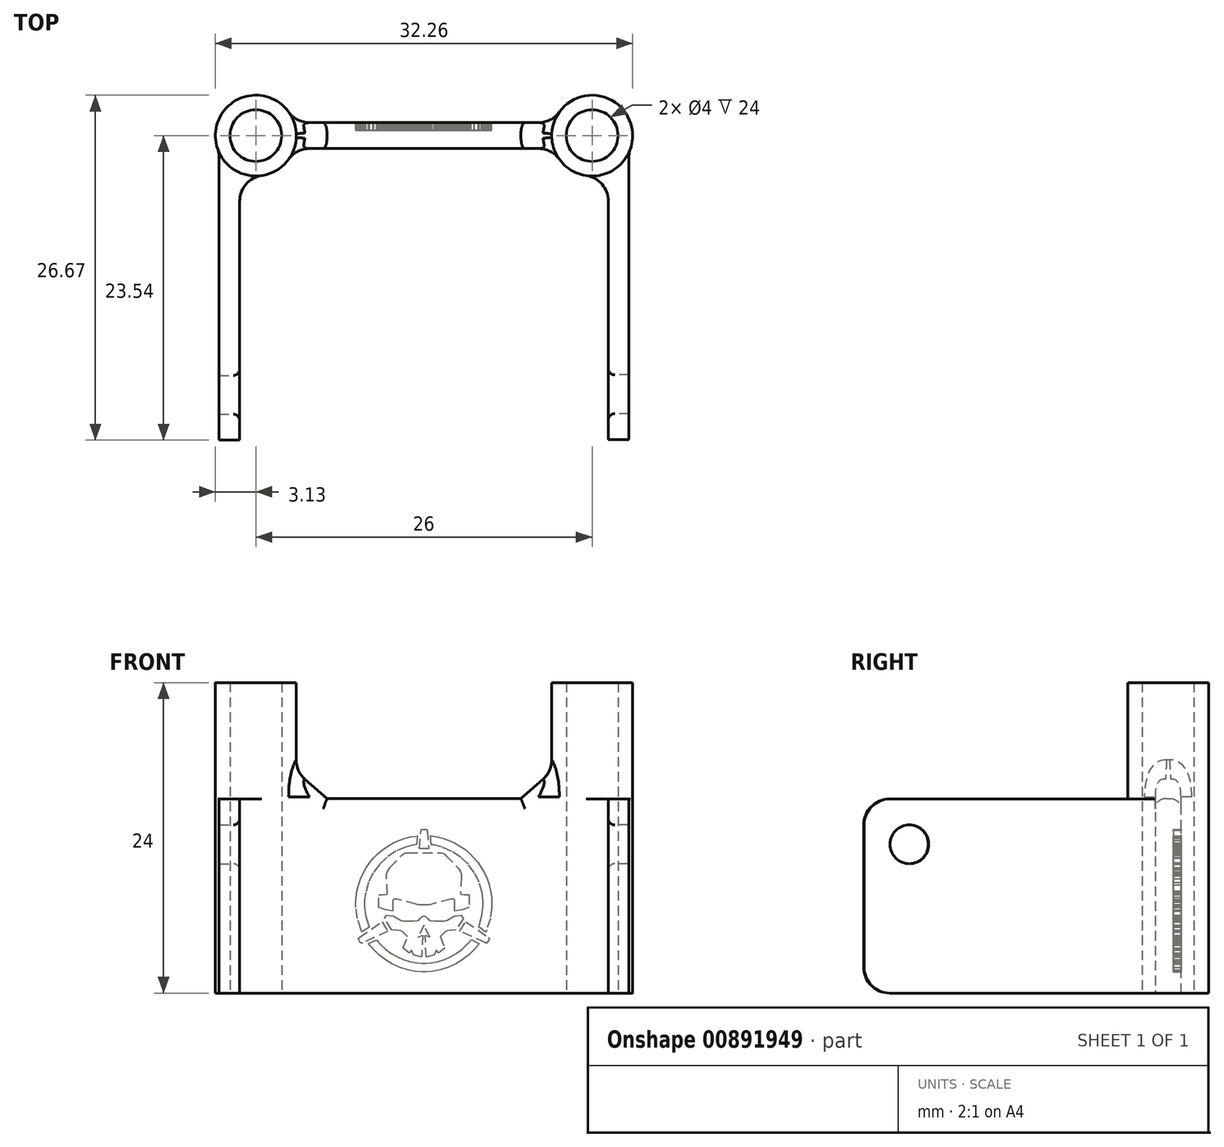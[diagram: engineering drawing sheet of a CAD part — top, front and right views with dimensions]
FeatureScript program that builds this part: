
annotation { "Feature Type Name" : "Feature", "Feature Type Description" : "" }
export const myFeature = defineFeature(function(context is Context, id is Id, definition is map)
    precondition{}
    {
        {
            var Q0;
            Q0=qCreatedBy(makeId("Top.planeOp"),FACE);
            var sketch = newSketch(context, id + "F0", { "sketchPlane" : qUnion([Q0])});
            skCircle(sketch, "E0", {"center": v(-13, 0) * mm, "radius": 3.12 * mm});
            skCircle(sketch, "E1", {"center": v(13, 0) * mm, "radius": 3.12 * mm});
            skSolve(sketch);
        }
        {
            var Q0;
            Q0=qSketchRegion(id+"F0",true);
            extrude(context, id + "F1", {"entities" : qUnion([Q0]), "depth" : 24 * mm});
        }
        {
            var Q0;
            Q0=qCreatedBy(makeId("Front.planeOp"),FACE);
            var sketch = newSketch(context, id + "F2", { "sketchPlane" : qUnion([Q0])});
            skLineSegment(sketch, "E2", {"start": v(12, 0) * mm, "end": v(12, 19) * mm});
            skLineSegment(sketch, "E3", {"start": v(12, 19) * mm, "end": v(12, 19) * mm});
            skLineSegment(sketch, "E4", {"start": v(12, 19) * mm, "end": v(7.5, 15.03) * mm});
            skLineSegment(sketch, "E5", {"start": v(7.5, 15.03) * mm, "end": v(-7.5, 15.03) * mm});
            skLineSegment(sketch, "E6", {"start": v(-7.5, 15.03) * mm, "end": v(-12, 19) * mm});
            skLineSegment(sketch, "E7", {"start": v(-12, 19) * mm, "end": v(-12, 0) * mm});
            skLineSegment(sketch, "E8", {"start": v(-12, 0) * mm, "end": v(12, 0) * mm});
            skSolve(sketch);
        }
        {
            var Q0;
            Q0=makeQuery(id+"F2.imprint","IMPRINT",FACE,{"disambiguationData":[TD([[makeQuery(id+"F2.imprint","IMPRINT",EDGE,{"derivedFrom":sQuery(id+"F2.wireOp",EDGE,"E2")}),1.0]])]});
            extrude(context, id + "F3", {"entities" : qUnion([Q0]), "depth" : 2 * mm, "symmetric" : true});
        }
        {
            var Q0;
            Q0=qCreatedBy(makeId("Right.planeOp"),FACE);
            var Q1;
            Q1=qBodyType(qCreatedBy(id+"F5",EDGE),BodyType.WIRE);
            cPlane(context, id + "F4", {"entities" : qUnion([Q0, Q1]), "cplaneType" : CPlaneType.OFFSET, "offset" : 14.25 * mm, "width" : 150 * mm, "height" : 150 * mm});
        }
        {
            var Q0;
            Q0=qCreatedBy(id+"F4.planeOp",FACE);
            var sketch = newSketch(context, id + "F5", { "sketchPlane" : qUnion([Q0])});
            skCircle(sketch, "E9", {"center": v(-20, 11.5) * mm, "radius": 1.5 * mm});
            skLineSegment(sketch, "E10", {"start": v(0, 0) * mm, "end": v(-21.5, 0) * mm});
            skLineSegment(sketch, "E11", {"start": v(-23.5, 2) * mm, "end": v(-23.5, 13) * mm});
            skLineSegment(sketch, "E12", {"start": v(-21.5, 15) * mm, "end": v(0, 15) * mm});
            skLineSegment(sketch, "E13", {"start": v(0, 15) * mm, "end": v(0, 0) * mm});
            skPoint(sketch, "E14.visualSharp", {"position": v(-23.5, 15) * mm});
            skArc(sketch, "E14.filletArc", {"start": v(-21.5, 15) * mm, "mid": v(-22.91, 14.41) * mm, "end": v(-23.5, 13) * mm});
            skPoint(sketch, "E15.visualSharp", {"position": v(-23.5, 0) * mm});
            skArc(sketch, "E15.filletArc", {"start": v(-23.5, 2) * mm, "mid": v(-22.91, 0.59) * mm, "end": v(-21.5, 0) * mm});
            skSolve(sketch);
        }
        {
            var Q0;
            Q0=qSketchRegion(id+"F5",true);
            extrude(context, id + "F6", {"entities" : qUnion([Q0]), "operationType" : NewBodyOperationType.ADD, "depth" : 1.6 * mm});
        }
        {
            var Q0;
            Q0=qCreatedBy(makeId("Right.planeOp"),FACE);
            cPlane(context, id + "F7", {"entities" : qUnion([Q0]), "cplaneType" : CPlaneType.OFFSET, "offset" : 14.25 * mm, "oppositeDirection" : true, "width" : 150 * mm, "height" : 150 * mm});
        }
        {
            var Q0;
            Q0=qCreatedBy(id+"F7.planeOp",FACE);
            var sketch = newSketch(context, id + "F8", { "sketchPlane" : qUnion([Q0])});
            skCircle(sketch, "E16", {"center": v(-20.04, 11.5) * mm, "radius": 1.5 * mm});
            skLineSegment(sketch, "E17", {"start": v(-0.04, 0) * mm, "end": v(-21.54, 0) * mm});
            skLineSegment(sketch, "E18", {"start": v(-23.54, 2) * mm, "end": v(-23.54, 13) * mm});
            skLineSegment(sketch, "E19", {"start": v(-21.54, 15) * mm, "end": v(-0.04, 15) * mm});
            skLineSegment(sketch, "E20", {"start": v(-0.04, 15) * mm, "end": v(-0.04, 0) * mm});
            skPoint(sketch, "E21.visualSharp", {"position": v(-23.54, 15) * mm});
            skArc(sketch, "E21.filletArc", {"start": v(-21.54, 15) * mm, "mid": v(-22.95, 14.41) * mm, "end": v(-23.54, 13) * mm});
            skPoint(sketch, "E22.visualSharp", {"position": v(-23.54, 0) * mm});
            skArc(sketch, "E22.filletArc", {"start": v(-23.54, 2) * mm, "mid": v(-22.95, 0.59) * mm, "end": v(-21.54, 0) * mm});
            skSolve(sketch);
        }
        {
            var Q0;
            Q0=qSketchRegion(id+"F8",true);
            extrude(context, id + "F9", {"entities" : qUnion([Q0]), "operationType" : NewBodyOperationType.ADD, "oppositeDirection" : true, "depth" : 1.6 * mm});
        }
        {
            var Q0;
            Q0=qCreatedBy(makeId("Top.planeOp"),FACE);
            var sketch = newSketch(context, id + "F10", { "sketchPlane" : qUnion([Q0])});
            skCircle(sketch, "E23", {"center": v(-13, 0) * mm, "radius": 0.5 * mm});
            skCircle(sketch, "E24", {"center": v(13, 0) * mm, "radius": 1.75 * mm});
            skSolve(sketch);
        }
        {
            var Q0;
            Q0=sQuery(id+"F10.wireOp",VERTEX,"E23.center");
            var Q1;
            Q1=sQuery(id+"F10.wireOp",VERTEX,"E24.center");
            var Q2;
            Q2=makeQuery(id+"F1.opExtrude","SWEPT_BODY",BODY,{"disambiguationData":[OSD([sQuery(id+"F0.wireOp",EDGE,"E0")])]});
            var Q3;
            Q3=makeQuery(id+"F3.opExtrude","SWEPT_BODY",BODY,{"disambiguationData":[OSD([sQuery(id+"F2.wireOp",EDGE,"in345Lub-D59E-tOme-60dj-Cq3KucnByxKd"),sQuery(id+"F2.wireOp",EDGE,"E2"),sQuery(id+"F2.wireOp",EDGE,"E4"),sQuery(id+"F2.wireOp",EDGE,"E5"),sQuery(id+"F2.wireOp",EDGE,"E6"),sQuery(id+"F2.wireOp",EDGE,"E7")])]});
            var Q4;
            Q4=makeQuery(id+"FYRTTrcSvXfLMjP_3.opExtrude","SWEPT_BODY",BODY,{"disambiguationData":[OSD([sQuery(id+"Fs8EBPNxBlUYa75_3.wireOp",EDGE,"JWLeMf17-8jiZ-tYXv-UtJK-ccR32AaEOkmf.bottom"),sQuery(id+"Fs8EBPNxBlUYa75_3.wireOp",EDGE,"JWLeMf17-8jiZ-tYXv-UtJK-ccR32AaEOkmf.top"),sQuery(id+"Fs8EBPNxBlUYa75_3.wireOp",EDGE,"JWLeMf17-8jiZ-tYXv-UtJK-ccR32AaEOkmf.left"),sQuery(id+"Fs8EBPNxBlUYa75_3.wireOp",EDGE,"JWLeMf17-8jiZ-tYXv-UtJK-ccR32AaEOkmf.right")])]});
            var Q5;
            Q5=makeQuery(id+"F1.opExtrude","SWEPT_BODY",BODY,{"disambiguationData":[OSD([sQuery(id+"F0.wireOp",EDGE,"E1")])]});
            var Q6;
            Q6=makeQuery(id+"FYRTTrcSvXfLMjP_3.opExtrude","SWEPT_BODY",BODY,{"disambiguationData":[OSD([sQuery(id+"Fs8EBPNxBlUYa75_3.wireOp",EDGE,"dHJZYZbQ-VqZX-6sAW-GdeU-ZCC2gI22Ho79.bottom"),sQuery(id+"Fs8EBPNxBlUYa75_3.wireOp",EDGE,"dHJZYZbQ-VqZX-6sAW-GdeU-ZCC2gI22Ho79.top"),sQuery(id+"Fs8EBPNxBlUYa75_3.wireOp",EDGE,"dHJZYZbQ-VqZX-6sAW-GdeU-ZCC2gI22Ho79.left"),sQuery(id+"Fs8EBPNxBlUYa75_3.wireOp",EDGE,"dHJZYZbQ-VqZX-6sAW-GdeU-ZCC2gI22Ho79.right")])]});
            hole(context, id + "F11", {"style" : HoleStyle.SIMPLE, "endStyle" : HoleEndStyle.THROUGH, "oppositeDirection" : true, "holeDiameter" : 4 * mm, "isTappedThrough" : true, "tappedDepth" : 12 * mm, "tapClearance" : 3, "locations" : qUnion([Q0, Q1]), "scope" : qUnion([Q2, Q3, Q4, Q5, Q6])});
        }
        {
            var Q0;
            Q0=makeQuery(id+"F1.opExtrude","SWEPT_BODY",BODY,{"disambiguationData":[OSD([sQuery(id+"F0.wireOp",EDGE,"E1")])]});
            var Q1;
            Q1=makeQuery(id+"F3.opExtrude","SWEPT_BODY",BODY,{"disambiguationData":[OSD([sQuery(id+"F2.wireOp",EDGE,"in345Lub-D59E-tOme-60dj-Cq3KucnByxKd"),sQuery(id+"F2.wireOp",EDGE,"E2"),sQuery(id+"F2.wireOp",EDGE,"E4"),sQuery(id+"F2.wireOp",EDGE,"E5"),sQuery(id+"F2.wireOp",EDGE,"E6"),sQuery(id+"F2.wireOp",EDGE,"E7")])]});
            var Q2;
            Q2=makeQuery(id+"F1.opExtrude","SWEPT_BODY",BODY,{"disambiguationData":[OSD([sQuery(id+"F0.wireOp",EDGE,"E0")])]});
            booleanBodies(context, id + "F12", {"operationType" : BooleanOperationType.UNION, "tools" : qUnion([Q0, Q1, Q2])});
        }
        {
            var Q0;
            Q0=makeQuery(id+"F3.opExtrude","CAP_EDGE",EDGE,{"disambiguationData":[OSD([sQuery(id+"F2.wireOp",EDGE,"E5")])],"isStart":false});
            var Q1;
            Q1=makeQuery(id+"F3.opExtrude","CAP_EDGE",EDGE,{"disambiguationData":[OSD([sQuery(id+"F2.wireOp",EDGE,"E5")])],"isStart":true});
            var Q2;
            Q2=makeQuery(id+"F3.opExtrude","CAP_EDGE",EDGE,{"disambiguationData":[OSD([sQuery(id+"F2.wireOp",EDGE,"E6")])],"isStart":false});
            var Q3;
            Q3=makeQuery(id+"F3.opExtrude","CAP_EDGE",EDGE,{"disambiguationData":[OSD([sQuery(id+"F2.wireOp",EDGE,"E6")])],"isStart":true});
            var Q4;
            Q4=makeQuery(id+"F3.opExtrude","CAP_EDGE",EDGE,{"disambiguationData":[OSD([sQuery(id+"F2.wireOp",EDGE,"E4")])],"isStart":false});
            var Q5;
            Q5=makeQuery(id+"F3.opExtrude","CAP_EDGE",EDGE,{"disambiguationData":[OSD([sQuery(id+"F2.wireOp",EDGE,"E4")])],"isStart":true});
            fillet(context, id + "F13", {"entities" : qUnion([Q0, Q1, Q2, Q3, Q4, Q5]), "radius" : .8 * mm, "tangentPropagation" : true, "allowEdgeOverflow" : false});
        }
        {
            var Q0;
            Q0=makeQuery(id+"F11.hole-0.boolean.opBoolean","INTERSECT",EDGE,{"derivedFrom":[makeQuery(id+"F1.opExtrude","CAP_FACE",FACE,{"disambiguationData":[OSD([sQuery(id+"F0.wireOp",EDGE,"E0")])],"isStart":false}),makeQuery(id+"F11.hole-0.opRevolve","SWEPT_FACE",FACE,{"disambiguationData":[OSD([sQuery(id+"F11.hole-0.sketch.wireOp",EDGE,"core_line_2")])]})]});
            var Q1;
            Q1=makeQuery(id+"F11.hole-1.boolean.opBoolean","INTERSECT",EDGE,{"derivedFrom":[makeQuery(id+"F1.opExtrude","CAP_FACE",FACE,{"disambiguationData":[OSD([sQuery(id+"F0.wireOp",EDGE,"E1")])],"isStart":false}),makeQuery(id+"F11.hole-1.opRevolve","SWEPT_FACE",FACE,{"disambiguationData":[OSD([sQuery(id+"F11.hole-1.sketch.wireOp",EDGE,"core_line_2")])]})]});
            var Q2;
            Q2=makeQuery(id+"F9.opExtrude","CAP_EDGE",EDGE,{"disambiguationData":[OSD([sQuery(id+"F8.wireOp",EDGE,"E16")])],"isStart":true});
            var Q3;
            Q3=makeQuery(id+"F6.opExtrude","CAP_EDGE",EDGE,{"disambiguationData":[OSD([sQuery(id+"F5.wireOp",EDGE,"E9")])],"isStart":true});
            fillet(context, id + "F14", {"entities" : qUnion([Q0, Q1, Q2, Q3]), "radius" : .5 * mm, "tangentPropagation" : true, "allowEdgeOverflow" : false});
        }
        {
            var Q0;
            Q0=makeQuery(id+"F3.opExtrude","CAP_FACE",FACE,{"disambiguationData":[OSD([sQuery(id+"F2.wireOp",EDGE,"E2"),sQuery(id+"F2.wireOp",EDGE,"E4"),sQuery(id+"F2.wireOp",EDGE,"E5"),sQuery(id+"F2.wireOp",EDGE,"E6"),sQuery(id+"F2.wireOp",EDGE,"E7"),sQuery(id+"F2.wireOp",EDGE,"E8")])],"isStart":true});
            var sketch = newSketch(context, id + "F15", { "sketchPlane" : qUnion([Q0])});
            skLineSegment(sketch, "E25", {"start": v(-0.2, 12.65) * mm, "end": v(-0.2, 12.64) * mm});
            skLineSegment(sketch, "E26", {"start": v(-0.2, 12.64) * mm, "end": v(-0.23, 12.63) * mm});
            skLineSegment(sketch, "E27", {"start": v(-0.23, 12.63) * mm, "end": v(-0.24, 12.59) * mm});
            skLineSegment(sketch, "E28", {"start": v(-0.24, 12.59) * mm, "end": v(-0.24, 12.58) * mm});
            skLineSegment(sketch, "E29", {"start": v(-0.24, 12.58) * mm, "end": v(-0.38, 11.17) * mm});
            skLineSegment(sketch, "E30", {"start": v(-0.38, 11.17) * mm, "end": v(0.36, 11.17) * mm});
            skLineSegment(sketch, "E31", {"start": v(0.36, 11.17) * mm, "end": v(0.22, 12.58) * mm});
            skLineSegment(sketch, "E32", {"start": v(0.22, 12.58) * mm, "end": v(0.22, 12.59) * mm});
            skLineSegment(sketch, "E33", {"start": v(0.22, 12.59) * mm, "end": v(0.2, 12.63) * mm});
            skLineSegment(sketch, "E34", {"start": v(0.2, 12.63) * mm, "end": v(0.19, 12.64) * mm});
            skLineSegment(sketch, "E35", {"start": v(0.19, 12.64) * mm, "end": v(0.18, 12.65) * mm});
            skLineSegment(sketch, "E36", {"start": v(0.18, 12.65) * mm, "end": v(-0.2, 12.65) * mm});
            skLineSegment(sketch, "E37", {"start": v(-0.5, 12.15) * mm, "end": v(-0.63, 12.13) * mm});
            skLineSegment(sketch, "E38", {"start": v(-0.63, 12.13) * mm, "end": v(-1, 12.07) * mm});
            skLineSegment(sketch, "E39", {"start": v(-1, 12.07) * mm, "end": v(-1.48, 11.96) * mm});
            skLineSegment(sketch, "E40", {"start": v(-1.48, 11.96) * mm, "end": v(-1.94, 11.8) * mm});
            skLineSegment(sketch, "E41", {"start": v(-1.94, 11.8) * mm, "end": v(-2.38, 11.6) * mm});
            skLineSegment(sketch, "E42", {"start": v(-2.38, 11.6) * mm, "end": v(-2.8, 11.36) * mm});
            skLineSegment(sketch, "E43", {"start": v(-2.8, 11.36) * mm, "end": v(-3.19, 11.09) * mm});
            skLineSegment(sketch, "E44", {"start": v(-3.19, 11.09) * mm, "end": v(-3.55, 10.78) * mm});
            skLineSegment(sketch, "E45", {"start": v(-3.55, 10.78) * mm, "end": v(-3.89, 10.44) * mm});
            skLineSegment(sketch, "E46", {"start": v(-3.89, 10.44) * mm, "end": v(-4.19, 10.08) * mm});
            skLineSegment(sketch, "E47", {"start": v(-4.19, 10.08) * mm, "end": v(-4.46, 9.69) * mm});
            skLineSegment(sketch, "E48", {"start": v(-4.46, 9.69) * mm, "end": v(-4.69, 9.27) * mm});
            skLineSegment(sketch, "E49", {"start": v(-4.69, 9.27) * mm, "end": v(-4.88, 8.83) * mm});
            skLineSegment(sketch, "E50", {"start": v(-4.88, 8.83) * mm, "end": v(-5.04, 8.38) * mm});
            skLineSegment(sketch, "E51", {"start": v(-5.04, 8.38) * mm, "end": v(-5.15, 7.9) * mm});
            skLineSegment(sketch, "E52", {"start": v(-5.15, 7.9) * mm, "end": v(-5.22, 7.41) * mm});
            skLineSegment(sketch, "E53", {"start": v(-5.22, 7.41) * mm, "end": v(-5.25, 7.04) * mm});
            skLineSegment(sketch, "E54", {"start": v(-5.25, 7.04) * mm, "end": v(-5.25, 6.9) * mm});
            skLineSegment(sketch, "E55", {"start": v(-5.25, 6.9) * mm, "end": v(-5.25, 6.63) * mm});
            skLineSegment(sketch, "E56", {"start": v(-5.25, 6.63) * mm, "end": v(-5.12, 5.77) * mm});
            skLineSegment(sketch, "E57", {"start": v(-5.12, 5.77) * mm, "end": v(-4.85, 4.89) * mm});
            skLineSegment(sketch, "E58", {"start": v(-4.85, 4.89) * mm, "end": v(-4.77, 4.72) * mm});
            skLineSegment(sketch, "E59", {"start": v(-4.77, 4.72) * mm, "end": v(-4.22, 5.12) * mm});
            skLineSegment(sketch, "E60", {"start": v(-4.22, 5.12) * mm, "end": v(-4.28, 5.25) * mm});
            skLineSegment(sketch, "E61", {"start": v(-4.28, 5.25) * mm, "end": v(-4.49, 5.98) * mm});
            skLineSegment(sketch, "E62", {"start": v(-4.49, 5.98) * mm, "end": v(-4.58, 6.68) * mm});
            skLineSegment(sketch, "E63", {"start": v(-4.58, 6.68) * mm, "end": v(-4.58, 6.9) * mm});
            skLineSegment(sketch, "E64", {"start": v(-4.58, 6.9) * mm, "end": v(-4.58, 7.12) * mm});
            skLineSegment(sketch, "E65", {"start": v(-4.58, 7.12) * mm, "end": v(-4.5, 7.76) * mm});
            skLineSegment(sketch, "E66", {"start": v(-4.5, 7.76) * mm, "end": v(-4.28, 8.56) * mm});
            skLineSegment(sketch, "E67", {"start": v(-4.28, 8.56) * mm, "end": v(-3.91, 9.3) * mm});
            skLineSegment(sketch, "E68", {"start": v(-3.91, 9.3) * mm, "end": v(-3.43, 9.95) * mm});
            skLineSegment(sketch, "E69", {"start": v(-3.43, 9.95) * mm, "end": v(-2.84, 10.5) * mm});
            skLineSegment(sketch, "E70", {"start": v(-2.84, 10.5) * mm, "end": v(-2.16, 10.96) * mm});
            skLineSegment(sketch, "E71", {"start": v(-2.16, 10.96) * mm, "end": v(-1.4, 11.28) * mm});
            skLineSegment(sketch, "E72", {"start": v(-1.4, 11.28) * mm, "end": v(-0.78, 11.44) * mm});
            skLineSegment(sketch, "E73", {"start": v(-0.78, 11.44) * mm, "end": v(-0.57, 11.46) * mm});
            skLineSegment(sketch, "E74", {"start": v(-0.57, 11.46) * mm, "end": v(-0.5, 12.15) * mm});
            skLineSegment(sketch, "E75", {"start": v(0.52, 12.14) * mm, "end": v(0.58, 11.47) * mm});
            skLineSegment(sketch, "E76", {"start": v(0.58, 11.47) * mm, "end": v(0.79, 11.44) * mm});
            skLineSegment(sketch, "E77", {"start": v(0.79, 11.44) * mm, "end": v(1.4, 11.28) * mm});
            skLineSegment(sketch, "E78", {"start": v(1.4, 11.28) * mm, "end": v(2.17, 10.96) * mm});
            skLineSegment(sketch, "E79", {"start": v(2.17, 10.96) * mm, "end": v(2.86, 10.5) * mm});
            skLineSegment(sketch, "E80", {"start": v(2.86, 10.5) * mm, "end": v(3.45, 9.95) * mm});
            skLineSegment(sketch, "E81", {"start": v(3.45, 9.95) * mm, "end": v(3.93, 9.3) * mm});
            skLineSegment(sketch, "E82", {"start": v(3.93, 9.3) * mm, "end": v(4.3, 8.56) * mm});
            skLineSegment(sketch, "E83", {"start": v(4.3, 8.56) * mm, "end": v(4.52, 7.76) * mm});
            skLineSegment(sketch, "E84", {"start": v(4.52, 7.76) * mm, "end": v(4.6, 7.12) * mm});
            skLineSegment(sketch, "E85", {"start": v(4.6, 7.12) * mm, "end": v(4.6, 6.9) * mm});
            skLineSegment(sketch, "E86", {"start": v(4.6, 6.9) * mm, "end": v(4.6, 6.68) * mm});
            skLineSegment(sketch, "E87", {"start": v(4.6, 6.68) * mm, "end": v(4.5, 5.98) * mm});
            skLineSegment(sketch, "E88", {"start": v(4.5, 5.98) * mm, "end": v(4.3, 5.25) * mm});
            skLineSegment(sketch, "E89", {"start": v(4.3, 5.25) * mm, "end": v(4.23, 5.11) * mm});
            skLineSegment(sketch, "E90", {"start": v(4.23, 5.11) * mm, "end": v(4.78, 4.71) * mm});
            skLineSegment(sketch, "E91", {"start": v(4.78, 4.71) * mm, "end": v(4.86, 4.88) * mm});
            skLineSegment(sketch, "E92", {"start": v(4.86, 4.88) * mm, "end": v(5.14, 5.77) * mm});
            skLineSegment(sketch, "E93", {"start": v(5.14, 5.77) * mm, "end": v(5.26, 6.62) * mm});
            skLineSegment(sketch, "E94", {"start": v(5.26, 6.62) * mm, "end": v(5.26, 6.9) * mm});
            skLineSegment(sketch, "E95", {"start": v(5.26, 6.9) * mm, "end": v(5.26, 7.04) * mm});
            skLineSegment(sketch, "E96", {"start": v(5.26, 7.04) * mm, "end": v(5.24, 7.41) * mm});
            skLineSegment(sketch, "E97", {"start": v(5.24, 7.41) * mm, "end": v(5.17, 7.9) * mm});
            skLineSegment(sketch, "E98", {"start": v(5.17, 7.9) * mm, "end": v(5.05, 8.37) * mm});
            skLineSegment(sketch, "E99", {"start": v(5.05, 8.37) * mm, "end": v(4.9, 8.83) * mm});
            skLineSegment(sketch, "E100", {"start": v(4.9, 8.83) * mm, "end": v(4.7, 9.27) * mm});
            skLineSegment(sketch, "E101", {"start": v(4.7, 9.27) * mm, "end": v(4.47, 9.68) * mm});
            skLineSegment(sketch, "E102", {"start": v(4.47, 9.68) * mm, "end": v(4.2, 10.08) * mm});
            skLineSegment(sketch, "E103", {"start": v(4.2, 10.08) * mm, "end": v(3.9, 10.44) * mm});
            skLineSegment(sketch, "E104", {"start": v(3.9, 10.44) * mm, "end": v(3.56, 10.78) * mm});
            skLineSegment(sketch, "E105", {"start": v(3.56, 10.78) * mm, "end": v(3.2, 11.08) * mm});
            skLineSegment(sketch, "E106", {"start": v(3.2, 11.08) * mm, "end": v(2.8, 11.36) * mm});
            skLineSegment(sketch, "E107", {"start": v(2.8, 11.36) * mm, "end": v(2.4, 11.6) * mm});
            skLineSegment(sketch, "E108", {"start": v(2.4, 11.6) * mm, "end": v(1.95, 11.8) * mm});
            skLineSegment(sketch, "E109", {"start": v(1.95, 11.8) * mm, "end": v(1.5, 11.95) * mm});
            skLineSegment(sketch, "E110", {"start": v(1.5, 11.95) * mm, "end": v(1.01, 12.07) * mm});
            skLineSegment(sketch, "E111", {"start": v(1.01, 12.07) * mm, "end": v(0.64, 12.13) * mm});
            skLineSegment(sketch, "E112", {"start": v(0.64, 12.13) * mm, "end": v(0.52, 12.14) * mm});
            skLineSegment(sketch, "E113", {"start": v(-1.2, 10.86) * mm, "end": v(-1.23, 10.86) * mm});
            skLineSegment(sketch, "E114", {"start": v(-1.23, 10.86) * mm, "end": v(-1.34, 10.84) * mm});
            skLineSegment(sketch, "E115", {"start": v(-1.34, 10.84) * mm, "end": v(-1.47, 10.8) * mm});
            skLineSegment(sketch, "E116", {"start": v(-1.47, 10.8) * mm, "end": v(-1.59, 10.75) * mm});
            skLineSegment(sketch, "E117", {"start": v(-1.59, 10.75) * mm, "end": v(-1.66, 10.69) * mm});
            skLineSegment(sketch, "E118", {"start": v(-1.66, 10.69) * mm, "end": v(-1.69, 10.66) * mm});
            skLineSegment(sketch, "E119", {"start": v(-1.69, 10.66) * mm, "end": v(-2.61, 9.7) * mm});
            skLineSegment(sketch, "E120", {"start": v(-2.61, 9.7) * mm, "end": v(-2.64, 9.67) * mm});
            skLineSegment(sketch, "E121", {"start": v(-2.64, 9.67) * mm, "end": v(-2.72, 9.56) * mm});
            skLineSegment(sketch, "E122", {"start": v(-2.72, 9.56) * mm, "end": v(-2.81, 9.39) * mm});
            skLineSegment(sketch, "E123", {"start": v(-2.81, 9.39) * mm, "end": v(-2.87, 9.2) * mm});
            skLineSegment(sketch, "E124", {"start": v(-2.87, 9.2) * mm, "end": v(-2.9, 9.05) * mm});
            skLineSegment(sketch, "E125", {"start": v(-2.9, 9.05) * mm, "end": v(-2.9, 9) * mm});
            skLineSegment(sketch, "E126", {"start": v(-2.9, 9) * mm, "end": v(-2.82, 7.67) * mm});
            skLineSegment(sketch, "E127", {"start": v(-2.82, 7.67) * mm, "end": v(-2.87, 7.65) * mm});
            skLineSegment(sketch, "E128", {"start": v(-2.87, 7.65) * mm, "end": v(-3.14, 7.6) * mm});
            skLineSegment(sketch, "E129", {"start": v(-3.14, 7.6) * mm, "end": v(-3.42, 7.6) * mm});
            skLineSegment(sketch, "E130", {"start": v(-3.42, 7.6) * mm, "end": v(-3.48, 7.6) * mm});
            skLineSegment(sketch, "E131", {"start": v(-3.48, 7.6) * mm, "end": v(-3.48, 6.61) * mm});
            skLineSegment(sketch, "E132", {"start": v(-3.48, 6.61) * mm, "end": v(-2.94, 6.42) * mm});
            skLineSegment(sketch, "E133", {"start": v(-2.94, 6.42) * mm, "end": v(-2.4, 6.35) * mm});
            skLineSegment(sketch, "E134", {"start": v(-2.4, 6.35) * mm, "end": v(-2.4, 7.11) * mm});
            skLineSegment(sketch, "E135", {"start": v(-2.4, 7.11) * mm, "end": v(-2.4, 7.13) * mm});
            skLineSegment(sketch, "E136", {"start": v(-2.4, 7.13) * mm, "end": v(-2.37, 7.2) * mm});
            skLineSegment(sketch, "E137", {"start": v(-2.37, 7.2) * mm, "end": v(-2.31, 7.25) * mm});
            skLineSegment(sketch, "E138", {"start": v(-2.31, 7.25) * mm, "end": v(-2.21, 7.27) * mm});
            skLineSegment(sketch, "E139", {"start": v(-2.21, 7.27) * mm, "end": v(-2.1, 7.27) * mm});
            skLineSegment(sketch, "E140", {"start": v(-2.1, 7.27) * mm, "end": v(-2.07, 7.26) * mm});
            skLineSegment(sketch, "E141", {"start": v(-2.07, 7.26) * mm, "end": v(-0.6, 6.87) * mm});
            skLineSegment(sketch, "E142", {"start": v(-0.6, 6.87) * mm, "end": v(-0.57, 6.86) * mm});
            skLineSegment(sketch, "E143", {"start": v(-0.57, 6.86) * mm, "end": v(-0.4, 6.82) * mm});
            skLineSegment(sketch, "E144", {"start": v(-0.4, 6.82) * mm, "end": v(-0.27, 6.8) * mm});
            skLineSegment(sketch, "E145", {"start": v(-0.27, 6.8) * mm, "end": v(-0.23, 6.8) * mm});
            skLineSegment(sketch, "E146", {"start": v(-0.23, 6.8) * mm, "end": v(0.24, 6.8) * mm});
            skLineSegment(sketch, "E147", {"start": v(0.24, 6.8) * mm, "end": v(0.29, 6.8) * mm});
            skLineSegment(sketch, "E148", {"start": v(0.29, 6.8) * mm, "end": v(0.42, 6.82) * mm});
            skLineSegment(sketch, "E149", {"start": v(0.42, 6.82) * mm, "end": v(0.58, 6.86) * mm});
            skLineSegment(sketch, "E150", {"start": v(0.58, 6.86) * mm, "end": v(0.61, 6.87) * mm});
            skLineSegment(sketch, "E151", {"start": v(0.61, 6.87) * mm, "end": v(2.08, 7.26) * mm});
            skLineSegment(sketch, "E152", {"start": v(2.08, 7.26) * mm, "end": v(2.12, 7.27) * mm});
            skLineSegment(sketch, "E153", {"start": v(2.12, 7.27) * mm, "end": v(2.23, 7.27) * mm});
            skLineSegment(sketch, "E154", {"start": v(2.23, 7.27) * mm, "end": v(2.33, 7.25) * mm});
            skLineSegment(sketch, "E155", {"start": v(2.33, 7.25) * mm, "end": v(2.39, 7.2) * mm});
            skLineSegment(sketch, "E156", {"start": v(2.39, 7.2) * mm, "end": v(2.4, 7.13) * mm});
            skLineSegment(sketch, "E157", {"start": v(2.4, 7.13) * mm, "end": v(2.4, 7.11) * mm});
            skLineSegment(sketch, "E158", {"start": v(2.4, 7.11) * mm, "end": v(2.4, 6.35) * mm});
            skLineSegment(sketch, "E159", {"start": v(2.4, 6.35) * mm, "end": v(2.96, 6.42) * mm});
            skLineSegment(sketch, "E160", {"start": v(2.96, 6.42) * mm, "end": v(3.5, 6.61) * mm});
            skLineSegment(sketch, "E161", {"start": v(3.5, 6.61) * mm, "end": v(3.5, 7.6) * mm});
            skLineSegment(sketch, "E162", {"start": v(3.5, 7.6) * mm, "end": v(3.44, 7.6) * mm});
            skLineSegment(sketch, "E163", {"start": v(3.44, 7.6) * mm, "end": v(3.16, 7.6) * mm});
            skLineSegment(sketch, "E164", {"start": v(3.16, 7.6) * mm, "end": v(2.89, 7.65) * mm});
            skLineSegment(sketch, "E165", {"start": v(2.89, 7.65) * mm, "end": v(2.84, 7.67) * mm});
            skLineSegment(sketch, "E166", {"start": v(2.84, 7.67) * mm, "end": v(2.9, 9) * mm});
            skLineSegment(sketch, "E167", {"start": v(2.9, 9) * mm, "end": v(2.9, 9.05) * mm});
            skLineSegment(sketch, "E168", {"start": v(2.9, 9.05) * mm, "end": v(2.89, 9.2) * mm});
            skLineSegment(sketch, "E169", {"start": v(2.89, 9.2) * mm, "end": v(2.83, 9.39) * mm});
            skLineSegment(sketch, "E170", {"start": v(2.83, 9.39) * mm, "end": v(2.73, 9.56) * mm});
            skLineSegment(sketch, "E171", {"start": v(2.73, 9.56) * mm, "end": v(2.66, 9.67) * mm});
            skLineSegment(sketch, "E172", {"start": v(2.66, 9.67) * mm, "end": v(2.63, 9.7) * mm});
            skLineSegment(sketch, "E173", {"start": v(2.63, 9.7) * mm, "end": v(1.7, 10.66) * mm});
            skLineSegment(sketch, "E174", {"start": v(1.7, 10.66) * mm, "end": v(1.68, 10.69) * mm});
            skLineSegment(sketch, "E175", {"start": v(1.68, 10.69) * mm, "end": v(1.6, 10.75) * mm});
            skLineSegment(sketch, "E176", {"start": v(1.6, 10.75) * mm, "end": v(1.49, 10.8) * mm});
            skLineSegment(sketch, "E177", {"start": v(1.49, 10.8) * mm, "end": v(1.36, 10.84) * mm});
            skLineSegment(sketch, "E178", {"start": v(1.36, 10.84) * mm, "end": v(1.24, 10.86) * mm});
            skLineSegment(sketch, "E179", {"start": v(1.24, 10.86) * mm, "end": v(1.2, 10.86) * mm});
            skLineSegment(sketch, "E180", {"start": v(1.2, 10.86) * mm, "end": v(-1.2, 10.86) * mm});
            skLineSegment(sketch, "E181", {"start": v(-2.87, 6.03) * mm, "end": v(-3.04, 5.77) * mm});
            skLineSegment(sketch, "E182", {"start": v(-3.04, 5.77) * mm, "end": v(-2.46, 4.87) * mm});
            skLineSegment(sketch, "E183", {"start": v(-2.46, 4.87) * mm, "end": v(-2.05, 4.85) * mm});
            skLineSegment(sketch, "E184", {"start": v(-2.05, 4.85) * mm, "end": v(-2, 4.85) * mm});
            skLineSegment(sketch, "E185", {"start": v(-2, 4.85) * mm, "end": v(-1.8, 4.83) * mm});
            skLineSegment(sketch, "E186", {"start": v(-1.8, 4.83) * mm, "end": v(-1.63, 4.76) * mm});
            skLineSegment(sketch, "E187", {"start": v(-1.63, 4.76) * mm, "end": v(-1.6, 4.73) * mm});
            skLineSegment(sketch, "E188", {"start": v(-1.6, 4.73) * mm, "end": v(-1.26, 4.38) * mm});
            skLineSegment(sketch, "E189", {"start": v(-1.26, 4.38) * mm, "end": v(-1.61, 3.48) * mm});
            skLineSegment(sketch, "E190", {"start": v(-1.61, 3.48) * mm, "end": v(-1.14, 3.1) * mm});
            skLineSegment(sketch, "E191", {"start": v(-1.14, 3.1) * mm, "end": v(-0.94, 3.31) * mm});
            skLineSegment(sketch, "E192", {"start": v(-0.94, 3.31) * mm, "end": v(-0.78, 2.93) * mm});
            skLineSegment(sketch, "E193", {"start": v(-0.78, 2.93) * mm, "end": v(-0.18, 2.77) * mm});
            skLineSegment(sketch, "E194", {"start": v(-0.18, 2.77) * mm, "end": v(-0.08, 4.48) * mm});
            skLineSegment(sketch, "E195", {"start": v(-0.08, 4.48) * mm, "end": v(-0.43, 4.33) * mm});
            skLineSegment(sketch, "E196", {"start": v(-0.43, 4.33) * mm, "end": v(0, 5.26) * mm});
            skLineSegment(sketch, "E197", {"start": v(0, 5.26) * mm, "end": v(0.45, 4.33) * mm});
            skLineSegment(sketch, "E198", {"start": v(0.45, 4.33) * mm, "end": v(0.1, 4.48) * mm});
            skLineSegment(sketch, "E199", {"start": v(0.1, 4.48) * mm, "end": v(0.2, 2.77) * mm});
            skLineSegment(sketch, "E200", {"start": v(0.2, 2.77) * mm, "end": v(0.8, 2.93) * mm});
            skLineSegment(sketch, "E201", {"start": v(0.8, 2.93) * mm, "end": v(0.95, 3.31) * mm});
            skLineSegment(sketch, "E202", {"start": v(0.95, 3.31) * mm, "end": v(1.15, 3.1) * mm});
            skLineSegment(sketch, "E203", {"start": v(1.15, 3.1) * mm, "end": v(1.63, 3.48) * mm});
            skLineSegment(sketch, "E204", {"start": v(1.63, 3.48) * mm, "end": v(1.27, 4.38) * mm});
            skLineSegment(sketch, "E205", {"start": v(1.27, 4.38) * mm, "end": v(1.62, 4.73) * mm});
            skLineSegment(sketch, "E206", {"start": v(1.62, 4.73) * mm, "end": v(1.65, 4.76) * mm});
            skLineSegment(sketch, "E207", {"start": v(1.65, 4.76) * mm, "end": v(1.82, 4.83) * mm});
            skLineSegment(sketch, "E208", {"start": v(1.82, 4.83) * mm, "end": v(2.02, 4.85) * mm});
            skLineSegment(sketch, "E209", {"start": v(2.02, 4.85) * mm, "end": v(2.07, 4.85) * mm});
            skLineSegment(sketch, "E210", {"start": v(2.07, 4.85) * mm, "end": v(2.48, 4.87) * mm});
            skLineSegment(sketch, "E211", {"start": v(2.48, 4.87) * mm, "end": v(3.06, 5.77) * mm});
            skLineSegment(sketch, "E212", {"start": v(3.06, 5.77) * mm, "end": v(2.88, 6.03) * mm});
            skLineSegment(sketch, "E213", {"start": v(2.88, 6.03) * mm, "end": v(2.35, 5.97) * mm});
            skLineSegment(sketch, "E214", {"start": v(2.35, 5.97) * mm, "end": v(1.82, 5.64) * mm});
            skLineSegment(sketch, "E215", {"start": v(1.82, 5.64) * mm, "end": v(1.75, 5.62) * mm});
            skLineSegment(sketch, "E216", {"start": v(1.75, 5.62) * mm, "end": v(1.53, 5.59) * mm});
            skLineSegment(sketch, "E217", {"start": v(1.53, 5.59) * mm, "end": v(1.2, 5.57) * mm});
            skLineSegment(sketch, "E218", {"start": v(1.2, 5.57) * mm, "end": v(0.83, 5.58) * mm});
            skLineSegment(sketch, "E219", {"start": v(0.83, 5.58) * mm, "end": v(0.5, 5.61) * mm});
            skLineSegment(sketch, "E220", {"start": v(0.5, 5.61) * mm, "end": v(0.4, 5.63) * mm});
            skLineSegment(sketch, "E221", {"start": v(0.4, 5.63) * mm, "end": v(0.38, 5.65) * mm});
            skLineSegment(sketch, "E222", {"start": v(0.38, 5.65) * mm, "end": v(0.33, 5.73) * mm});
            skLineSegment(sketch, "E223", {"start": v(0.33, 5.73) * mm, "end": v(0.23, 5.84) * mm});
            skLineSegment(sketch, "E224", {"start": v(0.23, 5.84) * mm, "end": v(0.12, 5.93) * mm});
            skLineSegment(sketch, "E225", {"start": v(0.12, 5.93) * mm, "end": v(0.04, 5.96) * mm});
            skLineSegment(sketch, "E226", {"start": v(0.04, 5.96) * mm, "end": v(0, 5.96) * mm});
            skLineSegment(sketch, "E227", {"start": v(0, 5.96) * mm, "end": v(-0.02, 5.96) * mm});
            skLineSegment(sketch, "E228", {"start": v(-0.02, 5.96) * mm, "end": v(-0.1, 5.93) * mm});
            skLineSegment(sketch, "E229", {"start": v(-0.1, 5.93) * mm, "end": v(-0.22, 5.84) * mm});
            skLineSegment(sketch, "E230", {"start": v(-0.22, 5.84) * mm, "end": v(-0.31, 5.73) * mm});
            skLineSegment(sketch, "E231", {"start": v(-0.31, 5.73) * mm, "end": v(-0.36, 5.65) * mm});
            skLineSegment(sketch, "E232", {"start": v(-0.36, 5.65) * mm, "end": v(-0.38, 5.63) * mm});
            skLineSegment(sketch, "E233", {"start": v(-0.38, 5.63) * mm, "end": v(-0.49, 5.61) * mm});
            skLineSegment(sketch, "E234", {"start": v(-0.49, 5.61) * mm, "end": v(-0.81, 5.58) * mm});
            skLineSegment(sketch, "E235", {"start": v(-0.81, 5.58) * mm, "end": v(-1.19, 5.57) * mm});
            skLineSegment(sketch, "E236", {"start": v(-1.19, 5.57) * mm, "end": v(-1.52, 5.59) * mm});
            skLineSegment(sketch, "E237", {"start": v(-1.52, 5.59) * mm, "end": v(-1.73, 5.62) * mm});
            skLineSegment(sketch, "E238", {"start": v(-1.73, 5.62) * mm, "end": v(-1.8, 5.64) * mm});
            skLineSegment(sketch, "E239", {"start": v(-1.8, 5.64) * mm, "end": v(-2.34, 5.97) * mm});
            skLineSegment(sketch, "E240", {"start": v(-2.34, 5.97) * mm, "end": v(-2.87, 6.03) * mm});
            skLineSegment(sketch, "E241", {"start": v(-3.23, 5.53) * mm, "end": v(-4.99, 4.3) * mm});
            skLineSegment(sketch, "E242", {"start": v(-4.99, 4.3) * mm, "end": v(-5, 4.28) * mm});
            skLineSegment(sketch, "E243", {"start": v(-5, 4.28) * mm, "end": v(-5.05, 4.24) * mm});
            skLineSegment(sketch, "E244", {"start": v(-5.05, 4.24) * mm, "end": v(-5.06, 4.2) * mm});
            skLineSegment(sketch, "E245", {"start": v(-5.06, 4.2) * mm, "end": v(-5.06, 4.2) * mm});
            skLineSegment(sketch, "E246", {"start": v(-5.06, 4.2) * mm, "end": v(-4.87, 3.86) * mm});
            skLineSegment(sketch, "E247", {"start": v(-4.87, 3.86) * mm, "end": v(-4.86, 3.86) * mm});
            skLineSegment(sketch, "E248", {"start": v(-4.86, 3.86) * mm, "end": v(-4.82, 3.85) * mm});
            skLineSegment(sketch, "E249", {"start": v(-4.82, 3.85) * mm, "end": v(-4.77, 3.87) * mm});
            skLineSegment(sketch, "E250", {"start": v(-4.77, 3.87) * mm, "end": v(-4.75, 3.88) * mm});
            skLineSegment(sketch, "E251", {"start": v(-4.75, 3.88) * mm, "end": v(-2.77, 4.8) * mm});
            skLineSegment(sketch, "E252", {"start": v(-2.77, 4.8) * mm, "end": v(-3.23, 5.53) * mm});
            skLineSegment(sketch, "E253", {"start": v(3.25, 5.53) * mm, "end": v(2.79, 4.8) * mm});
            skLineSegment(sketch, "E254", {"start": v(2.79, 4.8) * mm, "end": v(4.77, 3.88) * mm});
            skLineSegment(sketch, "E255", {"start": v(4.77, 3.88) * mm, "end": v(4.78, 3.87) * mm});
            skLineSegment(sketch, "E256", {"start": v(4.78, 3.87) * mm, "end": v(4.84, 3.85) * mm});
            skLineSegment(sketch, "E257", {"start": v(4.84, 3.85) * mm, "end": v(4.87, 3.86) * mm});
            skLineSegment(sketch, "E258", {"start": v(4.87, 3.86) * mm, "end": v(4.88, 3.86) * mm});
            skLineSegment(sketch, "E259", {"start": v(4.88, 3.86) * mm, "end": v(5.07, 4.2) * mm});
            skLineSegment(sketch, "E260", {"start": v(5.07, 4.2) * mm, "end": v(5.08, 4.2) * mm});
            skLineSegment(sketch, "E261", {"start": v(5.08, 4.2) * mm, "end": v(5.06, 4.24) * mm});
            skLineSegment(sketch, "E262", {"start": v(5.06, 4.24) * mm, "end": v(5.02, 4.28) * mm});
            skLineSegment(sketch, "E263", {"start": v(5.02, 4.28) * mm, "end": v(5, 4.3) * mm});
            skLineSegment(sketch, "E264", {"start": v(5, 4.3) * mm, "end": v(3.25, 5.53) * mm});
            skLineSegment(sketch, "E265", {"start": v(-3.65, 4.13) * mm, "end": v(-4.26, 3.84) * mm});
            skLineSegment(sketch, "E266", {"start": v(-4.26, 3.84) * mm, "end": v(-4.17, 3.72) * mm});
            skLineSegment(sketch, "E267", {"start": v(-4.17, 3.72) * mm, "end": v(-3.88, 3.37) * mm});
            skLineSegment(sketch, "E268", {"start": v(-3.88, 3.37) * mm, "end": v(-3.44, 2.94) * mm});
            skLineSegment(sketch, "E269", {"start": v(-3.44, 2.94) * mm, "end": v(-2.96, 2.56) * mm});
            skLineSegment(sketch, "E270", {"start": v(-2.96, 2.56) * mm, "end": v(-2.43, 2.25) * mm});
            skLineSegment(sketch, "E271", {"start": v(-2.43, 2.25) * mm, "end": v(-1.87, 2) * mm});
            skLineSegment(sketch, "E272", {"start": v(-1.87, 2) * mm, "end": v(-1.27, 1.8) * mm});
            skLineSegment(sketch, "E273", {"start": v(-1.27, 1.8) * mm, "end": v(-0.64, 1.69) * mm});
            skLineSegment(sketch, "E274", {"start": v(-0.64, 1.69) * mm, "end": v(-0.15, 1.65) * mm});
            skLineSegment(sketch, "E275", {"start": v(-0.15, 1.65) * mm, "end": v(0, 1.65) * mm});
            skLineSegment(sketch, "E276", {"start": v(0, 1.65) * mm, "end": v(0.17, 1.65) * mm});
            skLineSegment(sketch, "E277", {"start": v(0.17, 1.65) * mm, "end": v(0.66, 1.69) * mm});
            skLineSegment(sketch, "E278", {"start": v(0.66, 1.69) * mm, "end": v(1.28, 1.8) * mm});
            skLineSegment(sketch, "E279", {"start": v(1.28, 1.8) * mm, "end": v(1.88, 2) * mm});
            skLineSegment(sketch, "E280", {"start": v(1.88, 2) * mm, "end": v(2.44, 2.24) * mm});
            skLineSegment(sketch, "E281", {"start": v(2.44, 2.24) * mm, "end": v(2.97, 2.56) * mm});
            skLineSegment(sketch, "E282", {"start": v(2.97, 2.56) * mm, "end": v(3.45, 2.94) * mm});
            skLineSegment(sketch, "E283", {"start": v(3.45, 2.94) * mm, "end": v(3.9, 3.36) * mm});
            skLineSegment(sketch, "E284", {"start": v(3.9, 3.36) * mm, "end": v(4.19, 3.72) * mm});
            skLineSegment(sketch, "E285", {"start": v(4.19, 3.72) * mm, "end": v(4.28, 3.84) * mm});
            skLineSegment(sketch, "E286", {"start": v(4.28, 3.84) * mm, "end": v(3.66, 4.13) * mm});
            skLineSegment(sketch, "E287", {"start": v(3.66, 4.13) * mm, "end": v(3.58, 4.03) * mm});
            skLineSegment(sketch, "E288", {"start": v(3.58, 4.03) * mm, "end": v(3.33, 3.74) * mm});
            skLineSegment(sketch, "E289", {"start": v(3.33, 3.74) * mm, "end": v(2.95, 3.38) * mm});
            skLineSegment(sketch, "E290", {"start": v(2.95, 3.38) * mm, "end": v(2.53, 3.07) * mm});
            skLineSegment(sketch, "E291", {"start": v(2.53, 3.07) * mm, "end": v(2.08, 2.8) * mm});
            skLineSegment(sketch, "E292", {"start": v(2.08, 2.8) * mm, "end": v(1.6, 2.6) * mm});
            skLineSegment(sketch, "E293", {"start": v(1.6, 2.6) * mm, "end": v(1.1, 2.44) * mm});
            skLineSegment(sketch, "E294", {"start": v(1.1, 2.44) * mm, "end": v(0.56, 2.35) * mm});
            skLineSegment(sketch, "E295", {"start": v(0.56, 2.35) * mm, "end": v(0.15, 2.31) * mm});
            skLineSegment(sketch, "E296", {"start": v(0.15, 2.31) * mm, "end": v(0, 2.31) * mm});
            skLineSegment(sketch, "E297", {"start": v(0, 2.31) * mm, "end": v(-0.13, 2.31) * mm});
            skLineSegment(sketch, "E298", {"start": v(-0.13, 2.31) * mm, "end": v(-0.54, 2.35) * mm});
            skLineSegment(sketch, "E299", {"start": v(-0.54, 2.35) * mm, "end": v(-1.08, 2.44) * mm});
            skLineSegment(sketch, "E300", {"start": v(-1.08, 2.44) * mm, "end": v(-1.58, 2.6) * mm});
            skLineSegment(sketch, "E301", {"start": v(-1.58, 2.6) * mm, "end": v(-2.07, 2.8) * mm});
            skLineSegment(sketch, "E302", {"start": v(-2.07, 2.8) * mm, "end": v(-2.52, 3.07) * mm});
            skLineSegment(sketch, "E303", {"start": v(-2.52, 3.07) * mm, "end": v(-2.93, 3.38) * mm});
            skLineSegment(sketch, "E304", {"start": v(-2.93, 3.38) * mm, "end": v(-3.31, 3.74) * mm});
            skLineSegment(sketch, "E305", {"start": v(-3.31, 3.74) * mm, "end": v(-3.57, 4.03) * mm});
            skLineSegment(sketch, "E306", {"start": v(-3.57, 4.03) * mm, "end": v(-3.65, 4.13) * mm});
            skSolve(sketch);
        }
        {
            var Q0;
            Q0=qSketchRegion(id+"F15",true);
            extrude(context, id + "F16", {"entities" : qUnion([Q0]), "operationType" : NewBodyOperationType.REMOVE, "oppositeDirection" : true, "depth" : .6 * mm, "offsetDistance" : 25 * mm});
        }
        {
            var Q0;
            Q0=makeQuery(id+"F6.boolean.opBoolean","INTERSECT",EDGE,{"derivedFrom":[makeQuery(id+"F1.opExtrude","SWEPT_FACE",FACE,{"disambiguationData":[OSD([sQuery(id+"F0.wireOp",EDGE,"E1")])]}),makeQuery(id+"F6.opExtrude","CAP_FACE",FACE,{"disambiguationData":[OSD([sQuery(id+"F5.wireOp",EDGE,"E9"),sQuery(id+"F5.wireOp",EDGE,"E10"),sQuery(id+"F5.wireOp",EDGE,"E11"),sQuery(id+"F5.wireOp",EDGE,"E12"),sQuery(id+"F5.wireOp",EDGE,"E13"),sQuery(id+"F5.wireOp",EDGE,"E14.filletArc"),sQuery(id+"F5.wireOp",EDGE,"E15.filletArc")])],"isStart":true})]});
            var Q1;
            Q1=makeQuery(id+"F6.boolean.opBoolean","INTERSECT",EDGE,{"derivedFrom":[makeQuery(id+"F1.opExtrude","SWEPT_FACE",FACE,{"disambiguationData":[OSD([sQuery(id+"F0.wireOp",EDGE,"E1")])]}),makeQuery(id+"F6.opExtrude","CAP_FACE",FACE,{"disambiguationData":[OSD([sQuery(id+"F5.wireOp",EDGE,"E9"),sQuery(id+"F5.wireOp",EDGE,"E10"),sQuery(id+"F5.wireOp",EDGE,"E11"),sQuery(id+"F5.wireOp",EDGE,"E12"),sQuery(id+"F5.wireOp",EDGE,"E13"),sQuery(id+"F5.wireOp",EDGE,"E14.filletArc"),sQuery(id+"F5.wireOp",EDGE,"E15.filletArc")])],"isStart":false})]});
            var Q2;
            Q2=makeQuery(id+"F12.opBoolean","INTERSECT",EDGE,{"derivedFrom":[makeQuery(id+"F1.opExtrude","SWEPT_FACE",FACE,{"disambiguationData":[OSD([sQuery(id+"F0.wireOp",EDGE,"E1")])]}),makeQuery(id+"F3.opExtrude","CAP_FACE",FACE,{"disambiguationData":[OSD([sQuery(id+"F2.wireOp",EDGE,"E2"),sQuery(id+"F2.wireOp",EDGE,"E4"),sQuery(id+"F2.wireOp",EDGE,"E5"),sQuery(id+"F2.wireOp",EDGE,"E6"),sQuery(id+"F2.wireOp",EDGE,"E7"),sQuery(id+"F2.wireOp",EDGE,"E8")])],"isStart":false})]});
            var Q3;
            Q3=makeQuery(id+"F12.opBoolean","INTERSECT",EDGE,{"derivedFrom":[makeQuery(id+"F1.opExtrude","SWEPT_FACE",FACE,{"disambiguationData":[OSD([sQuery(id+"F0.wireOp",EDGE,"E0")])]}),makeQuery(id+"F3.opExtrude","CAP_FACE",FACE,{"disambiguationData":[OSD([sQuery(id+"F2.wireOp",EDGE,"E2"),sQuery(id+"F2.wireOp",EDGE,"E4"),sQuery(id+"F2.wireOp",EDGE,"E5"),sQuery(id+"F2.wireOp",EDGE,"E6"),sQuery(id+"F2.wireOp",EDGE,"E7"),sQuery(id+"F2.wireOp",EDGE,"E8")])],"isStart":false})]});
            var Q4;
            Q4=makeQuery(id+"F9.boolean.opBoolean","INTERSECT",EDGE,{"derivedFrom":[makeQuery(id+"F1.opExtrude","SWEPT_FACE",FACE,{"disambiguationData":[OSD([sQuery(id+"F0.wireOp",EDGE,"E0")])]}),makeQuery(id+"F9.opExtrude","CAP_FACE",FACE,{"disambiguationData":[OSD([sQuery(id+"F8.wireOp",EDGE,"E16"),sQuery(id+"F8.wireOp",EDGE,"E17"),sQuery(id+"F8.wireOp",EDGE,"E18"),sQuery(id+"F8.wireOp",EDGE,"E19"),sQuery(id+"F8.wireOp",EDGE,"E20"),sQuery(id+"F8.wireOp",EDGE,"E21.filletArc"),sQuery(id+"F8.wireOp",EDGE,"E22.filletArc")])],"isStart":false})]});
            var Q5;
            Q5=makeQuery(id+"F9.boolean.opBoolean","INTERSECT",EDGE,{"derivedFrom":[makeQuery(id+"F1.opExtrude","SWEPT_FACE",FACE,{"disambiguationData":[OSD([sQuery(id+"F0.wireOp",EDGE,"E0")])]}),makeQuery(id+"F9.opExtrude","CAP_FACE",FACE,{"disambiguationData":[OSD([sQuery(id+"F8.wireOp",EDGE,"E16"),sQuery(id+"F8.wireOp",EDGE,"E17"),sQuery(id+"F8.wireOp",EDGE,"E18"),sQuery(id+"F8.wireOp",EDGE,"E19"),sQuery(id+"F8.wireOp",EDGE,"E20"),sQuery(id+"F8.wireOp",EDGE,"E21.filletArc"),sQuery(id+"F8.wireOp",EDGE,"E22.filletArc")])],"isStart":true})]});
            fillet(context, id + "F17", {"entities" : qUnion([Q0, Q1, Q2, Q3, Q4, Q5]), "radius" : 2 * mm, "tangentPropagation" : true, "allowEdgeOverflow" : false});
        }
    });
